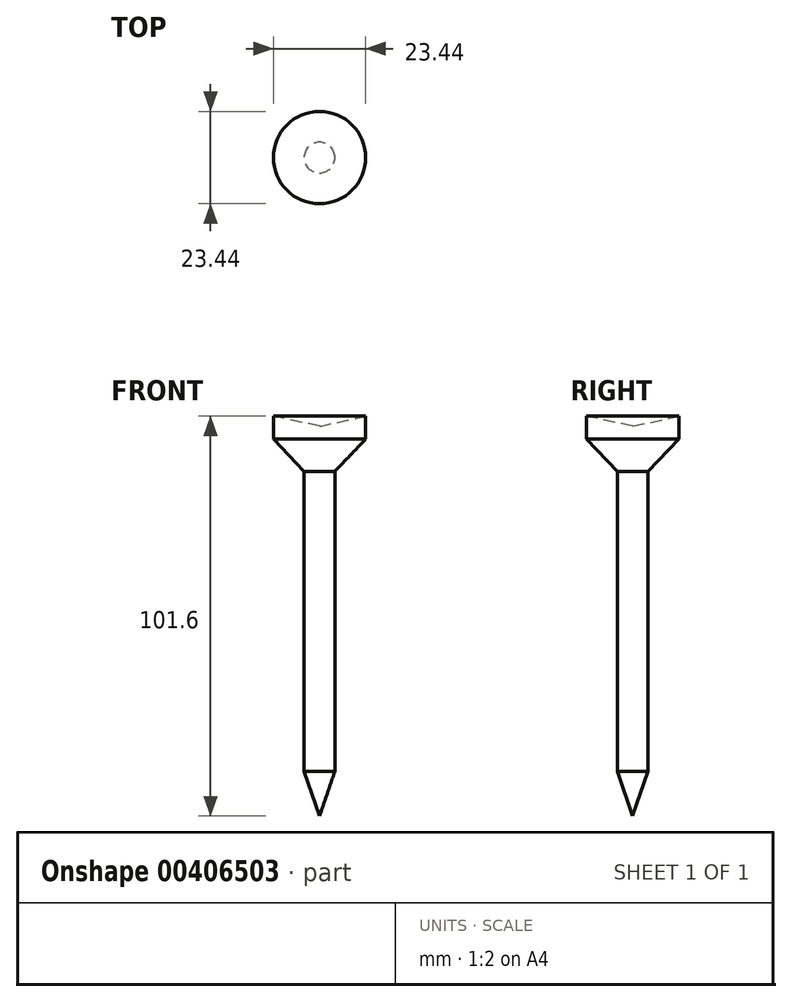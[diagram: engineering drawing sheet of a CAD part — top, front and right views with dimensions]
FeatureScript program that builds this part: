
annotation { "Feature Type Name" : "Feature", "Feature Type Description" : "" }
export const myFeature = defineFeature(function(context is Context, id is Id, definition is map)
    precondition{}
    {
        {
            var Q0;
            Q0=qCreatedBy(makeId("Front.planeOp"),FACE);
            var sketch = newSketch(context, id + "F0", { "sketchPlane" : qUnion([Q0])});
            skLineSegment(sketch, "E0", {"start": v(-11.72, 38.35) * mm, "end": v(-11.72, 34.06) * mm});
            skLineSegment(sketch, "E1", {"start": v(-11.72, 34.06) * mm, "end": v(-3.9, 25.85) * mm});
            skLineSegment(sketch, "E2", {"start": v(-3.9, 25.85) * mm, "end": v(-3.9, -50.35) * mm});
            skLineSegment(sketch, "E3", {"start": v(-3.9, -50.35) * mm, "end": v(0, -61.74) * mm});
            skLineSegment(sketch, "E4", {"start": v(0, 37.32) * mm, "end": v(0, -61.74) * mm});
            skLineSegment(sketch, "E5", {"start": v(0, 37.32) * mm, "end": v(-11.72, 39.86) * mm});
            skLineSegment(sketch, "E6", {"start": v(-11.72, 38.35) * mm, "end": v(-11.72, 39.86) * mm});
            skSolve(sketch);
        }
        {
            var Q0;
            Q0=makeQuery(id+"F0.imprint","IMPRINT",FACE,{"disambiguationData":[TD([[makeQuery(id+"F0.imprint","IMPRINT",EDGE,{"derivedFrom":sQuery(id+"F0.wireOp",EDGE,"E0")}),1.0]])]});
            var Q1;
            Q1=sQuery(id+"F0.wireOp",EDGE,"E4");
            revolve(context, id + "F1", {"entities" : qUnion([Q0]), "axis" : qUnion([Q1]), "revolveType" : RevolveType.FULL});
        }
    });
